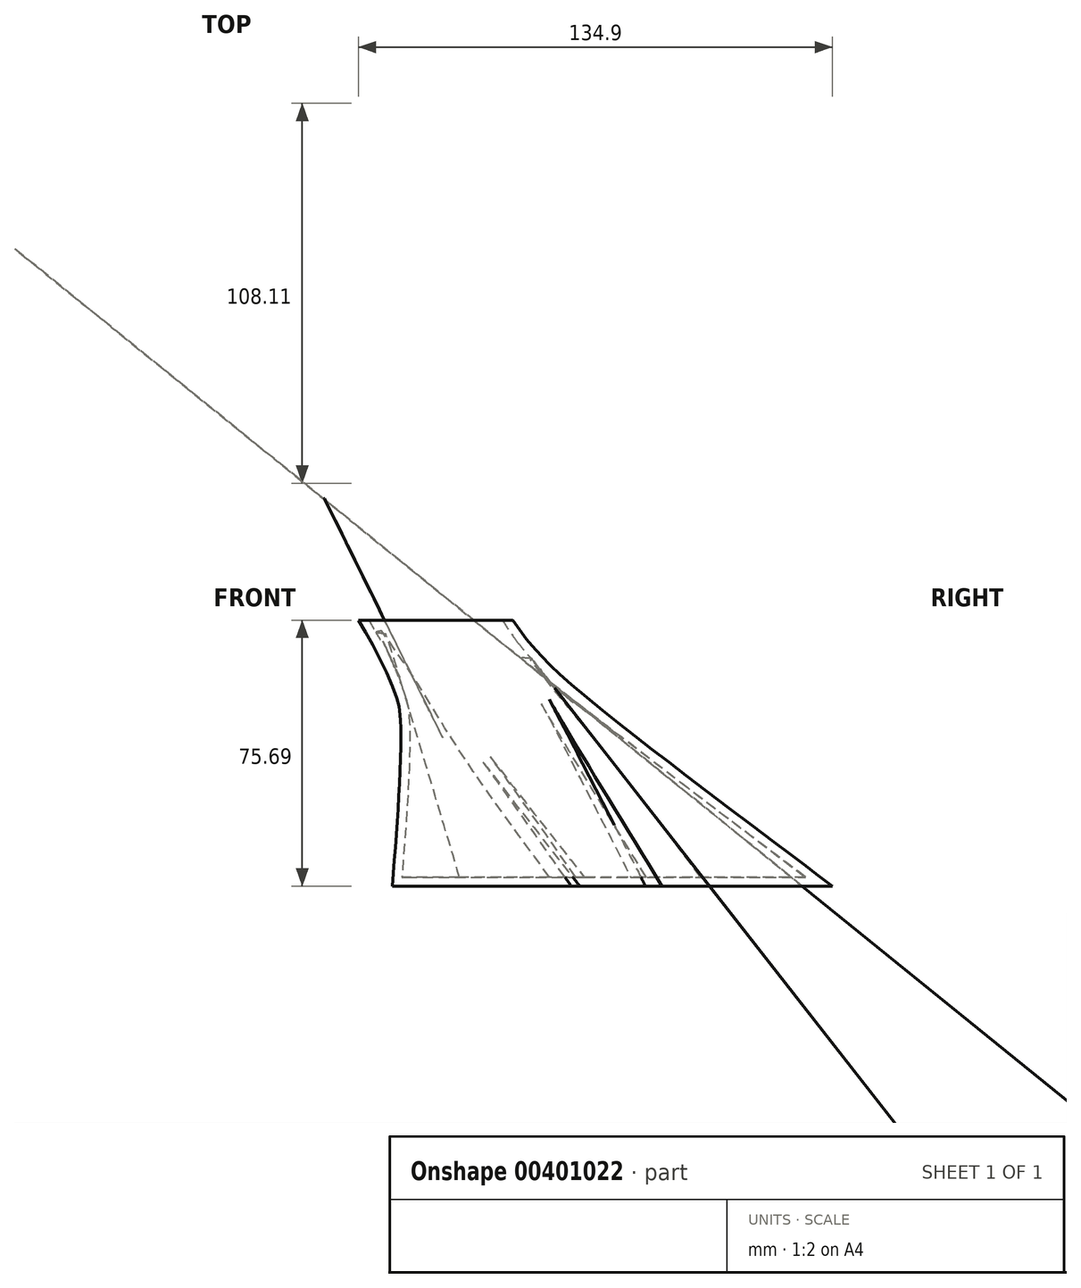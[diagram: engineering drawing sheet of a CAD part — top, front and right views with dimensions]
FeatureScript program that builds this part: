
annotation { "Feature Type Name" : "Feature", "Feature Type Description" : "" }
export const myFeature = defineFeature(function(context is Context, id is Id, definition is map)
    precondition{}
    {
        {
            var Q0;
            Q0=qCreatedBy(makeId("Top.planeOp"),FACE);
            cPlane(context, id + "F0", {"entities" : qUnion([Q0]), "cplaneType" : CPlaneType.OFFSET, "offset" : 75.7 * mm, "width" : 152.4 * mm, "height" : 152.4 * mm});
        }
        {
            var Q0;
            Q0=qCreatedBy(id+"F0.planeOp",FACE);
            var sketch = newSketch(context, id + "F1", { "sketchPlane" : qUnion([Q0])});
            skCircle(sketch, "E0", {"center": v(-50, 39) * mm, "radius": 22.01 * mm});
            skSolve(sketch);
        }
        {
            var Q0;
            Q0=qCreatedBy(makeId("Top.planeOp"),FACE);
            var sketch = newSketch(context, id + "F2", { "sketchPlane" : qUnion([Q0])});
            skFitSpline(sketch, "E1", {"points": [v(-60.87, -29.5) * mm, v(-22.89, -47.05) * mm, v(14.2, -36.21) * mm, v(9.67, -19.8) * mm, v(26.32, 0) * mm, v(53.68, -24) * mm, v(62.65, -13.88) * mm, v(38.47, 33.5) * mm, v(-9.72, 47.97) * mm, v(-9.24, 17.22) * mm, v(-17, 23.32) * mm, v(-34.68, 58.23) * mm, v(-51.57, 16.05) * mm, v(-60.87, -29.5) * mm]});
            skSolve(sketch);
        }
        {
            var Q0;
            Q0=makeQuery(id+"F2.imprint","IMPRINT",FACE,{"disambiguationData":[TD([[makeQuery(id+"F2.imprint","IMPRINT",EDGE,{"derivedFrom":sQuery(id+"F2.wireOp",EDGE,"E1")}),1.0]])]});
            var Q1;
            Q1=makeQuery(id+"F1.imprint","IMPRINT",FACE,{"disambiguationData":[TD([[makeQuery(id+"F1.imprint","IMPRINT",EDGE,{"derivedFrom":sQuery(id+"F1.wireOp",EDGE,"E0")}),1.0]])]});
            loft(context, id + "F3", {"sheetProfilesArray" : [{ "sheetProfileEntities" : qUnion([Q0]) }, { "sheetProfileEntities" : qUnion([Q1]) }]});
        }
        {
            var Q0;
            Q0=makeQuery(id+"F3.opLoft","CAP_FACE",FACE,{"disambiguationData":[OSD([makeQuery(id+"F1.imprint","IMPRINT",FACE,{"disambiguationData":[TD([[makeQuery(id+"F1.imprint","IMPRINT",EDGE,{"derivedFrom":sQuery(id+"F1.wireOp",EDGE,"E0")}),1.0]])]})])],"isStart":true});
            shell(context, id + "F4", {"entities" : qUnion([Q0]), "thickness" : 2.54 * mm});
        }
    });
